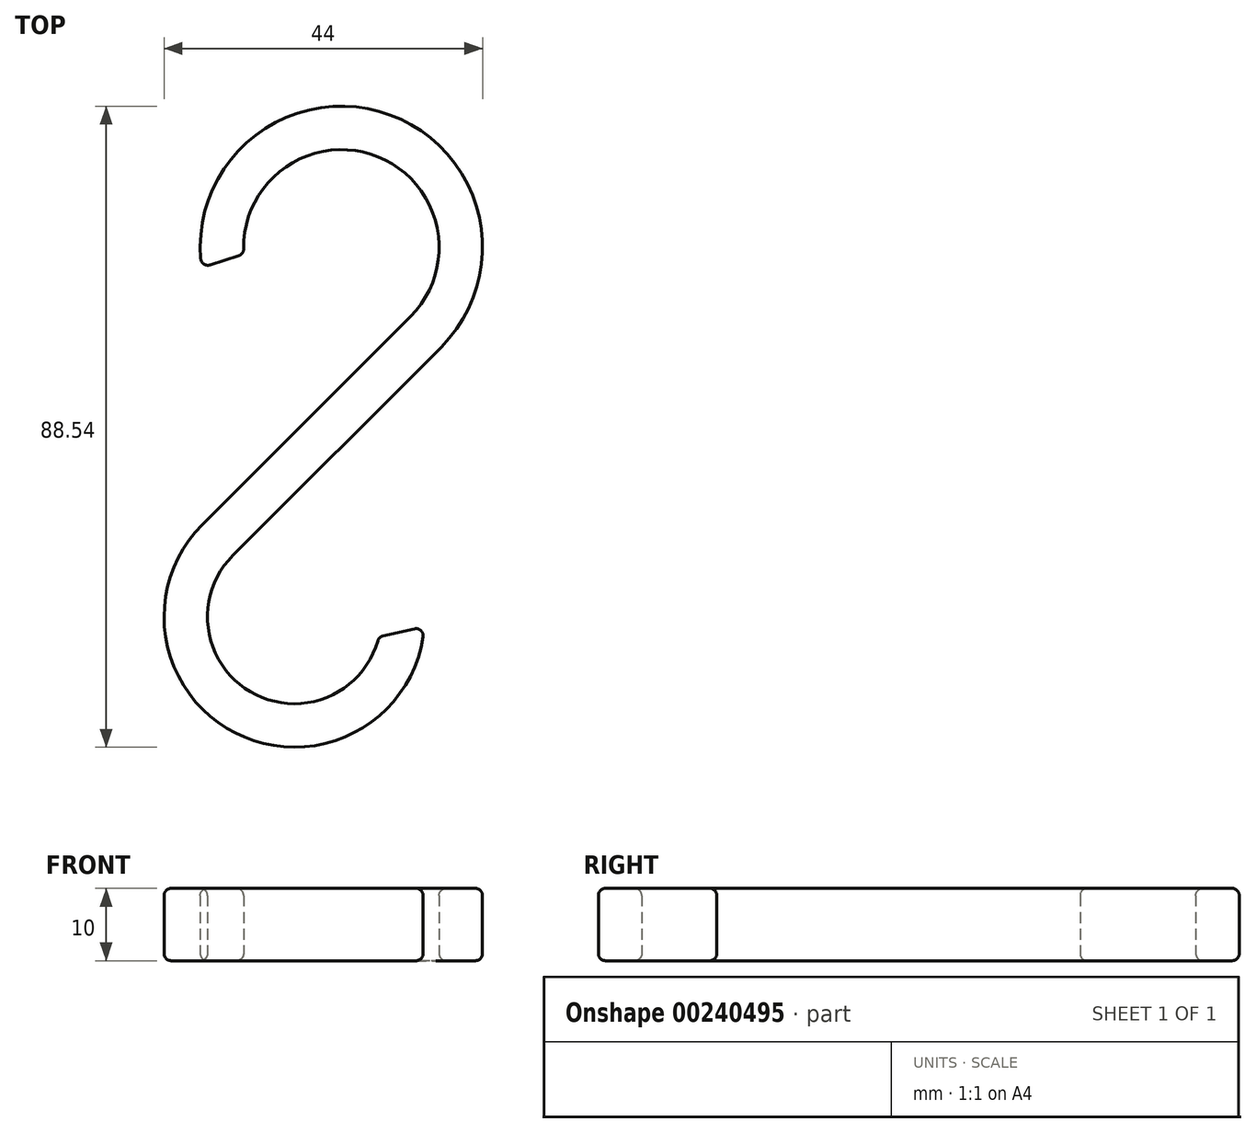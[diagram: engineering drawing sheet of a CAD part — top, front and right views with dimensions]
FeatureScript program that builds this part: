
annotation { "Feature Type Name" : "Feature", "Feature Type Description" : "" }
export const myFeature = defineFeature(function(context is Context, id is Id, definition is map)
    precondition{}
    {
        {
            var Q0;
            Q0=qCreatedBy(makeId("Top.planeOp"),FACE);
            var sketch = newSketch(context, id + "F0", { "sketchPlane" : qUnion([Q0])});
            skLineSegment(sketch, "E0", {"start": v(14.14, 14.14) * mm, "end": v(0, 0) * mm});
            skLineSegment(sketch, "E1", {"start": v(0, 0) * mm, "end": v(-14.62, -14.62) * mm});
            skArc(sketch, "E2", {"start": v(14.14, 14.14) * mm, "mid": v(9.32, 36.33) * mm, "end": v(-8.87, 22.75) * mm});
            skArc(sketch, "E3", {"start": v(-14.62, -14.62) * mm, "mid": v(-9.4, -43.71) * mm, "end": v(16.05, -28.69) * mm});
            skArc(sketch, "E4.0", {"start": v(18.38, 9.9) * mm, "mid": v(10.74, 42.2) * mm, "end": v(-14.7, 20.9) * mm});
            skLineSegment(sketch, "E4.1", {"start": v(18.38, 9.9) * mm, "end": v(4.24, -4.24) * mm});
            skLineSegment(sketch, "E4.2", {"start": v(4.24, -4.24) * mm, "end": v(-10.38, -18.87) * mm});
            skArc(sketch, "E4.3", {"start": v(-10.38, -18.87) * mm, "mid": v(-7.74, -37.83) * mm, "end": v(9.78, -30.1) * mm});
            skLineSegment(sketch, "E5", {"start": v(-8.87, 22.75) * mm, "end": v(-14.7, 20.9) * mm});
            skLineSegment(sketch, "E6", {"start": v(9.78, -30.1) * mm, "end": v(16.05, -28.69) * mm});
            skSolve(sketch);
        }
        {
            var Q0;
            Q0 = qSketchRegion(id + "F0", true);
            extrude(context, id + "F1", {"entities" : qUnion([Q0]), "depth" : 10 * mm});
        }
        {
            var Q0;
            Q0=makeQuery(id+"F1.opExtrude","SWEPT_EDGE",EDGE,{"disambiguationData":[OSD([sQuery(id+"F0.wireOp",EDGE,"E4.0"),sQuery(id+"F0.wireOp",EDGE,"E5")])]});
            var Q1;
            Q1=makeQuery(id+"F1.opExtrude","SWEPT_FACE",FACE,{"disambiguationData":[OSD([sQuery(id+"F0.wireOp",EDGE,"E5")])]});
            var Q2;
            Q2=makeQuery(id+"F1.opExtrude","SWEPT_FACE",FACE,{"disambiguationData":[OSD([sQuery(id+"F0.wireOp",EDGE,"E6")])]});
            var Q3;
            Q3=makeQuery(id+"F1.opExtrude","SWEPT_FACE",FACE,{"disambiguationData":[OSD([sQuery(id+"F0.wireOp",EDGE,"E2")])]});
            var Q4;
            Q4=makeQuery(id+"F1.opExtrude","SWEPT_FACE",FACE,{"disambiguationData":[OSD([sQuery(id+"F0.wireOp",EDGE,"E4.3")])]});
            fillet(context, id + "F2", {"entities" : qUnion([Q0, Q1, Q2, Q3, Q4]), "radius" : 1 * mm, "tangentPropagation" : true, "allowEdgeOverflow" : false});
        }
    });
